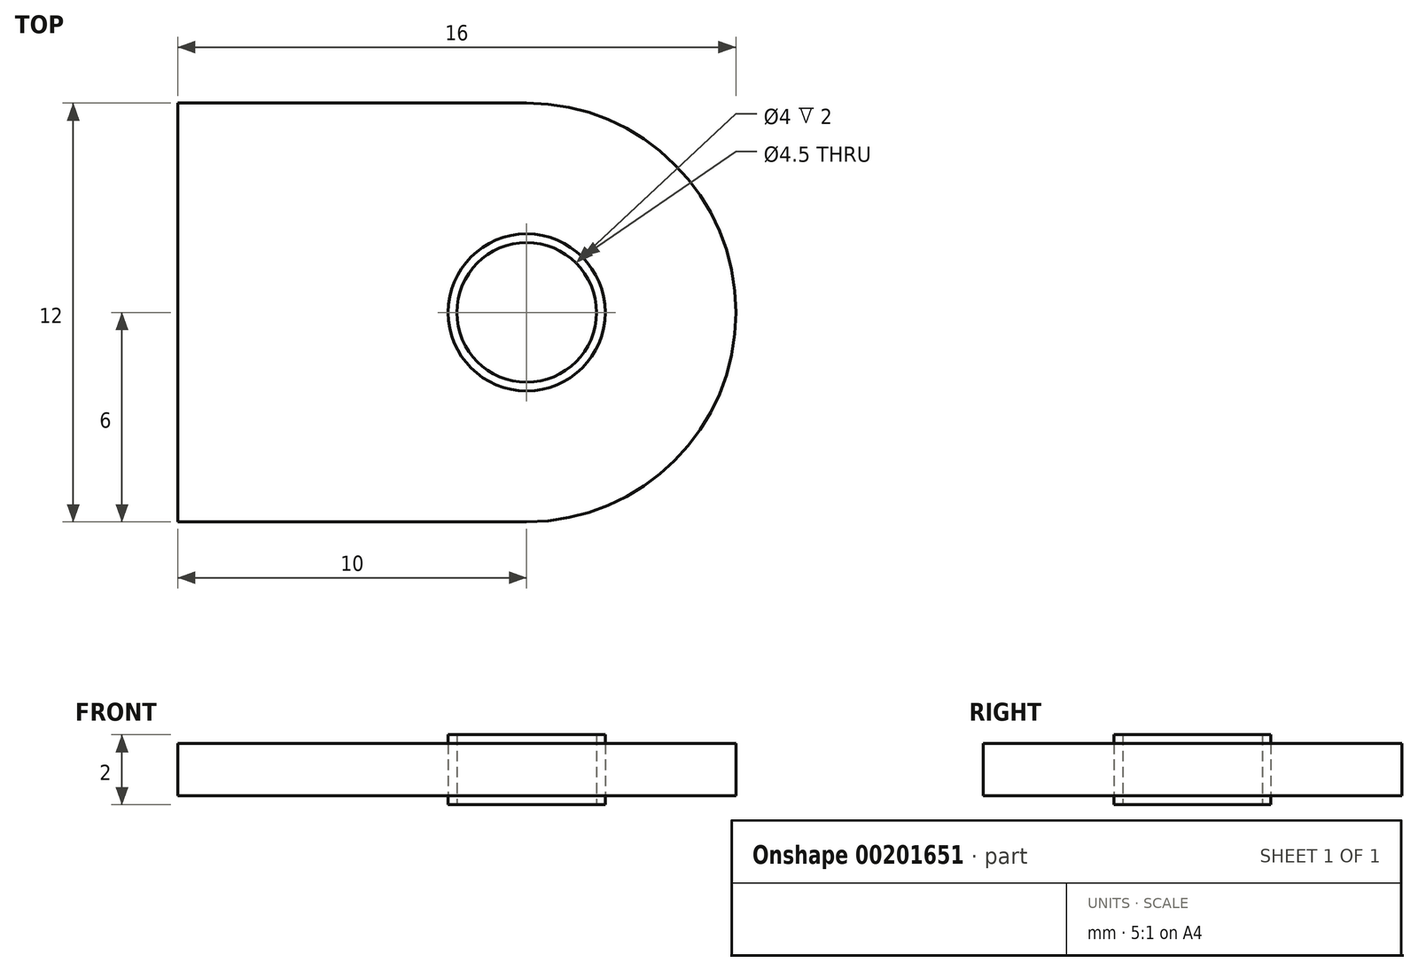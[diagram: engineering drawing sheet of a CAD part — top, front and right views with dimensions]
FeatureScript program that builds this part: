
annotation { "Feature Type Name" : "Feature", "Feature Type Description" : "" }
export const myFeature = defineFeature(function(context is Context, id is Id, definition is map)
    precondition{}
    {
        {
            var Q0;
            Q0=qCreatedBy(makeId("Top.planeOp"),FACE);
            var sketch = newSketch(context, id + "F0", { "sketchPlane" : qUnion([Q0])});
            skLineSegment(sketch, "E0", {"start": v(-8, -6) * mm, "end": v(-8, 6) * mm});
            skLineSegment(sketch, "E1", {"start": v(-8, -6) * mm, "end": v(2, -6) * mm});
            skLineSegment(sketch, "E2", {"start": v(-8, 6) * mm, "end": v(2, 6) * mm});
            skCircle(sketch, "E3", {"center": v(2, 0) * mm, "radius": 2.25 * mm});
            skArc(sketch, "E4", {"start": v(2, -6) * mm, "mid": v(8, 0) * mm, "end": v(2, 6) * mm});
            skCircle(sketch, "E5", {"center": v(2, 0) * mm, "radius": 2 * mm});
            skSolve(sketch);
        }
        {
            var Q0;
            Q0=makeQuery(id+"F0.imprint","IMPRINT",FACE,{"disambiguationData":[TD([[makeQuery(id+"F0.imprint","IMPRINT",EDGE,{"derivedFrom":sQuery(id+"F0.wireOp",EDGE,"E0")}),-1.0]])]});
            extrude(context, id + "F1", {"entities" : qUnion([Q0]), "endBound" : BoundingType.SYMMETRIC, "depth" : 1.5 * mm});
        }
        {
            var Q0;
            Q0=makeQuery(id+"F0.imprint","IMPRINT",FACE,{"disambiguationData":[TD([[makeQuery(id+"F0.imprint","IMPRINT",EDGE,{"derivedFrom":sQuery(id+"F0.wireOp",EDGE,"E5")}),-1.0]])]});
            extrude(context, id + "F2", {"entities" : qUnion([Q0]), "endBound" : BoundingType.SYMMETRIC, "depth" : 2 * mm});
        }
    });
